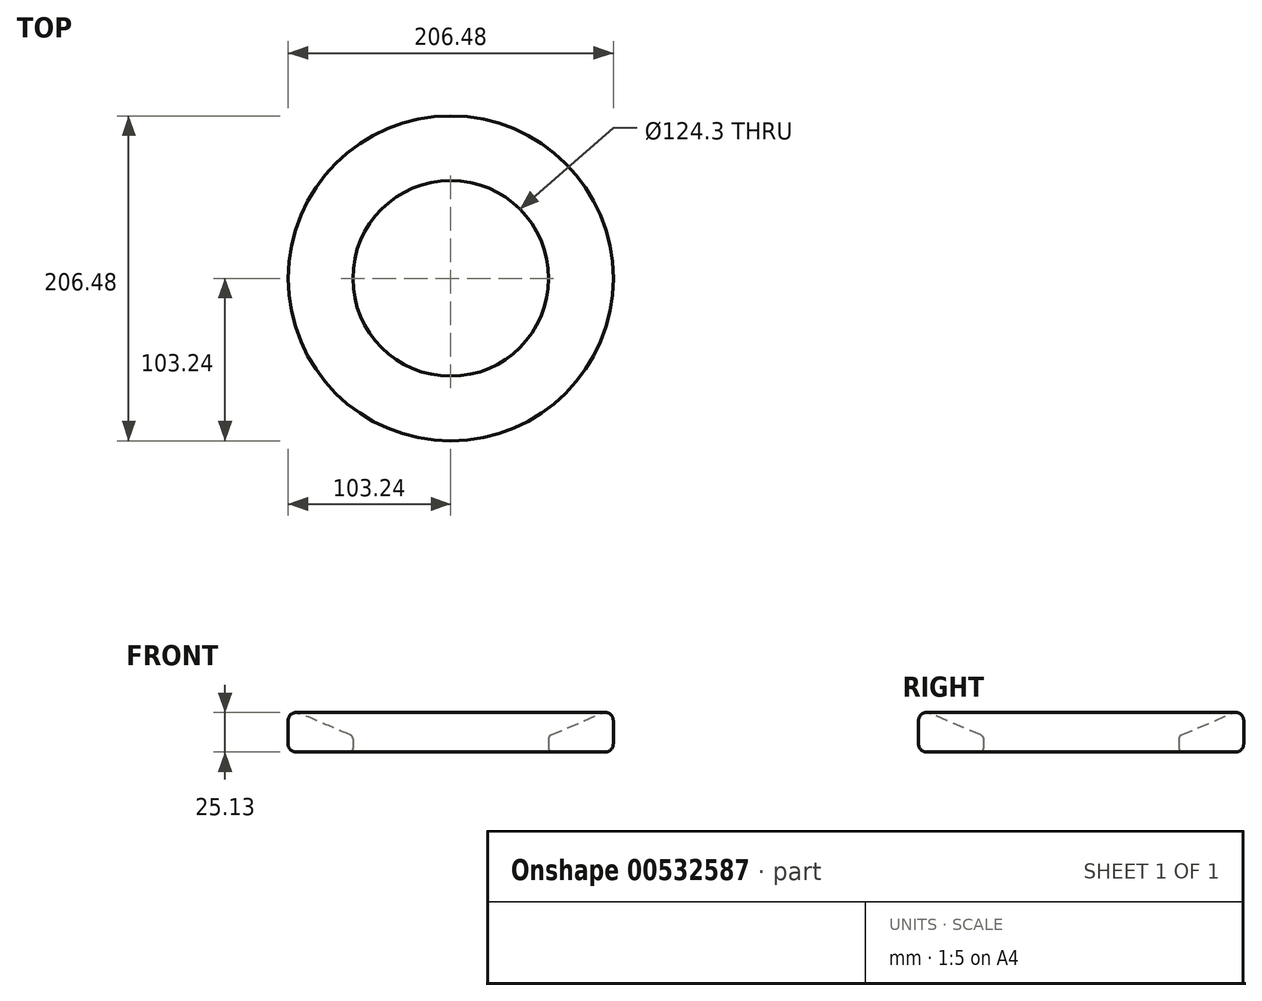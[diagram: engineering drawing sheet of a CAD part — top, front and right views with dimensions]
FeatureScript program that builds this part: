
annotation { "Feature Type Name" : "Feature", "Feature Type Description" : "" }
export const myFeature = defineFeature(function(context is Context, id is Id, definition is map)
    precondition{}
    {
        {
            var Q0;
            Q0=qCreatedBy(makeId("Top.planeOp"),FACE);
            var sketch = newSketch(context, id + "F0", { "sketchPlane" : qUnion([Q0])});
            skCircle(sketch, "E0", {"center": v(0, 0) * mm, "radius": 103.24 * mm});
            skCircle(sketch, "E1", {"center": v(0, 0) * mm, "radius": 62.15 * mm});
            skSolve(sketch);
        }
        {
            var Q0;
            Q0=makeQuery(id+"F0.imprint","IMPRINT",FACE,{"disambiguationData":[TD([[makeQuery(id+"F0.imprint","IMPRINT",EDGE,{"derivedFrom":sQuery(id+"F0.wireOp",EDGE,"E0")}),1.0]])]});
            extrude(context, id + "F1", {"entities" : qUnion([Q0]), "depth" : 25.4 * mm, "offsetDistance" : 25.4 * mm});
        }
        {
            var Q0;
            Q0=makeQuery(id+"F1.opExtrude","CAP_EDGE",EDGE,{"disambiguationData":[OSD([sQuery(id+"F0.wireOp",EDGE,"E1")])],"isStart":false});
            chamfer(context, id + "F2", {"entities" : qUnion([Q0]), "chamferType" : ChamferType.TWO_OFFSETS, "width1" : 15.24 * mm, "oppositeDirection" : false, "width2" : 35.56 * mm, "tangentPropagation" : true});
        }
        {
            var Q0;
            {var subQ0=sQuery(id+"F0.wireOp",EDGE,"E1");Q0=makeQuery(id+"F2.opChamfer","BLEND_EDGE",EDGE,{"blendedFrom":[makeQuery(id+"F1.opExtrude","CAP_EDGE",EDGE,{"disambiguationData":[OSD([subQ0])],"isStart":false}),makeQuery(id+"F1.opExtrude","CAP_FACE",FACE,{"disambiguationData":[OSD([sQuery(id+"F0.wireOp",EDGE,"E0"),subQ0])],"isStart":false})],"blendedInto":[makeQuery(id+"F1.opExtrude","CAP_FACE",FACE,{"disambiguationData":[OSD([sQuery(id+"F0.wireOp",EDGE,"E0"),subQ0])],"isStart":false})]});}
            fillet(context, id + "F3", {"entities" : qUnion([Q0]), "radius" : 10.16 * mm, "tangentPropagation" : true, "allowEdgeOverflow" : false});
        }
        {
            var Q0;
            Q0=makeQuery(id+"F1.opExtrude","CAP_EDGE",EDGE,{"disambiguationData":[OSD([sQuery(id+"F0.wireOp",EDGE,"E0")])],"isStart":false});
            fillet(context, id + "F4", {"entities" : qUnion([Q0]), "radius" : 5.08 * mm, "tangentPropagation" : true, "allowEdgeOverflow" : false});
        }
        {
            var Q0;
            {var subQ0=sQuery(id+"F0.wireOp",EDGE,"E1");Q0=makeQuery(id+"F2.opChamfer","BLEND_EDGE",EDGE,{"blendedFrom":[makeQuery(id+"F1.opExtrude","CAP_EDGE",EDGE,{"disambiguationData":[OSD([subQ0])],"isStart":false}),makeQuery(id+"F1.opExtrude","SWEPT_FACE",FACE,{"disambiguationData":[OSD([subQ0])]})],"blendedInto":[makeQuery(id+"F1.opExtrude","SWEPT_FACE",FACE,{"disambiguationData":[OSD([subQ0])]})]});}
            fillet(context, id + "F5", {"entities" : qUnion([Q0]), "radius" : 2.54 * mm, "tangentPropagation" : true, "allowEdgeOverflow" : false});
        }
        {
            var Q0;
            Q0=makeQuery(id+"F1.opExtrude","CAP_EDGE",EDGE,{"disambiguationData":[OSD([sQuery(id+"F0.wireOp",EDGE,"E0")])],"isStart":true});
            fillet(context, id + "F6", {"entities" : qUnion([Q0]), "radius" : 5.08 * mm, "tangentPropagation" : true, "allowEdgeOverflow" : false});
        }
        {
            var Q0;
            Q0=makeQuery(id+"F1.opExtrude","CAP_EDGE",EDGE,{"disambiguationData":[OSD([sQuery(id+"F0.wireOp",EDGE,"E1")])],"isStart":true});
            fillet(context, id + "F7", {"entities" : qUnion([Q0]), "radius" : 2.54 * mm, "tangentPropagation" : true, "allowEdgeOverflow" : false});
        }
    });
